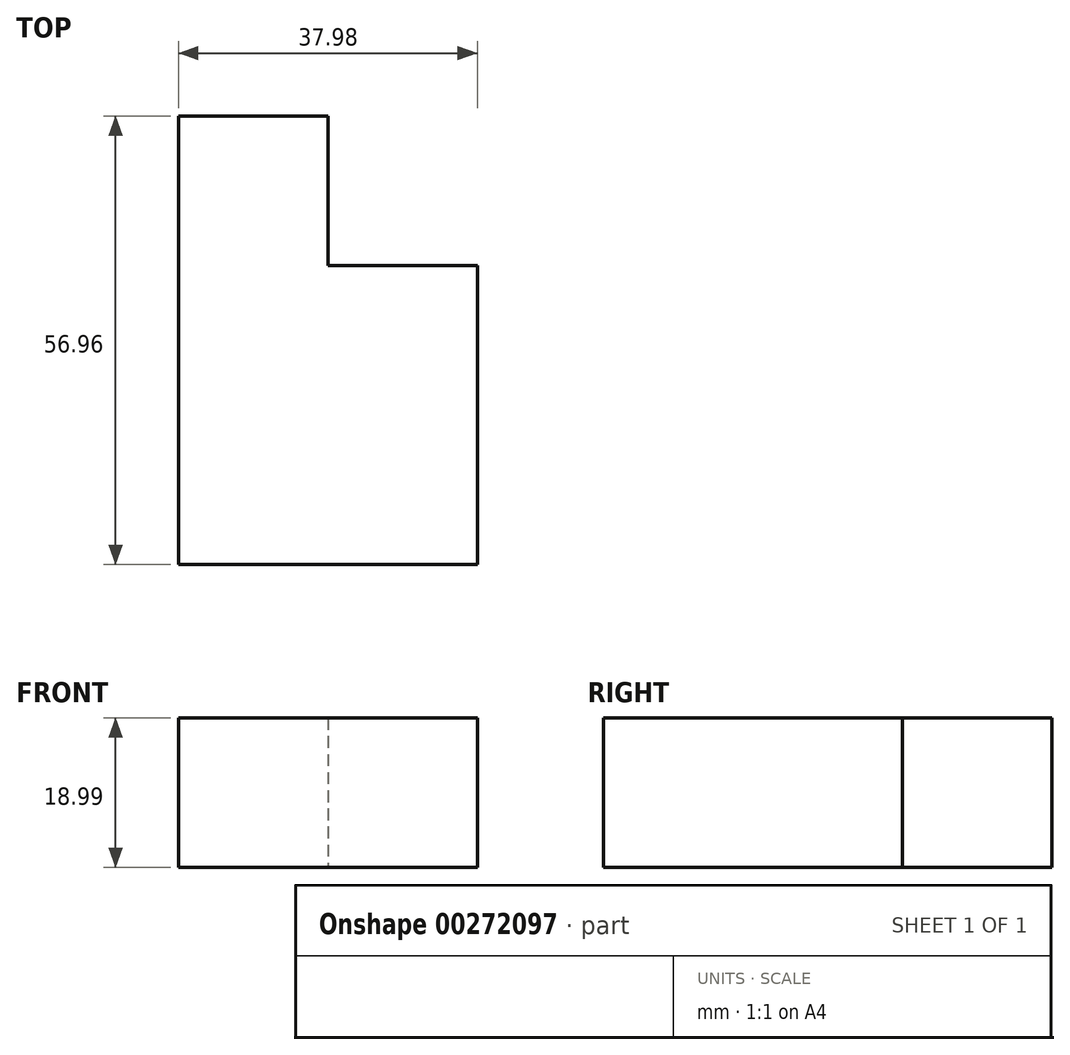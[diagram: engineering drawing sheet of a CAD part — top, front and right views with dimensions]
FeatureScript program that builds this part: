
annotation { "Feature Type Name" : "Feature", "Feature Type Description" : "" }
export const myFeature = defineFeature(function(context is Context, id is Id, definition is map)
    precondition{}
    {
        {
            var Q0;
            Q0=qCreatedBy(makeId("Top.planeOp"),FACE);
            var sketch = newSketch(context, id + "F0", { "sketchPlane" : qUnion([Q0])});
            skLineSegment(sketch, "E0.bottom", {"start": v(18.99, 18.99) * mm, "end": v(-18.99, 18.99) * mm});
            skLineSegment(sketch, "E0.top", {"start": v(18.99, -18.99) * mm, "end": v(-18.99, -18.99) * mm});
            skLineSegment(sketch, "E0.left", {"start": v(18.99, 18.99) * mm, "end": v(18.99, -18.99) * mm});
            skLineSegment(sketch, "E0.right", {"start": v(-18.99, 18.99) * mm, "end": v(-18.99, -18.99) * mm});
            skPoint(sketch, "E0.middle", {"position": v(0, 0) * mm});
            skSolve(sketch);
        }
        {
            var Q0;
            Q0=makeQuery(id+"F0.imprint","IMPRINT",FACE,{"disambiguationData":[TD([[makeQuery(id+"F0.imprint","IMPRINT",EDGE,{"derivedFrom":sQuery(id+"F0.wireOp",EDGE,"E0.bottom")}),1.0]])]});
            extrude(context, id + "F1", {"entities" : qUnion([Q0]), "depth" : 18.99 * mm});
        }
        {
            var Q0;
            Q0=makeQuery(id+"F1.opExtrude","SWEPT_FACE",FACE,{"disambiguationData":[OSD([sQuery(id+"F0.wireOp",EDGE,"E0.right")])]});
            var sketch = newSketch(context, id + "F2", { "sketchPlane" : qUnion([Q0])});
            skLineSegment(sketch, "E1.bottom", {"start": v(-18.99, 18.99) * mm, "end": v(-37.97, 18.99) * mm});
            skLineSegment(sketch, "E1.top", {"start": v(-18.99, 0) * mm, "end": v(-37.97, 0) * mm});
            skLineSegment(sketch, "E1.left", {"start": v(-18.99, 18.99) * mm, "end": v(-18.99, 0) * mm});
            skLineSegment(sketch, "E1.right", {"start": v(-37.97, 18.99) * mm, "end": v(-37.97, 0) * mm});
            skSolve(sketch);
        }
        {
            var Q0;
            Q0 = qSketchRegion(id + "F2", true);
            extrude(context, id + "F3", {"entities" : qUnion([Q0]), "operationType" : NewBodyOperationType.ADD, "oppositeDirection" : true, "depth" : 18.99 * mm});
        }
    });
